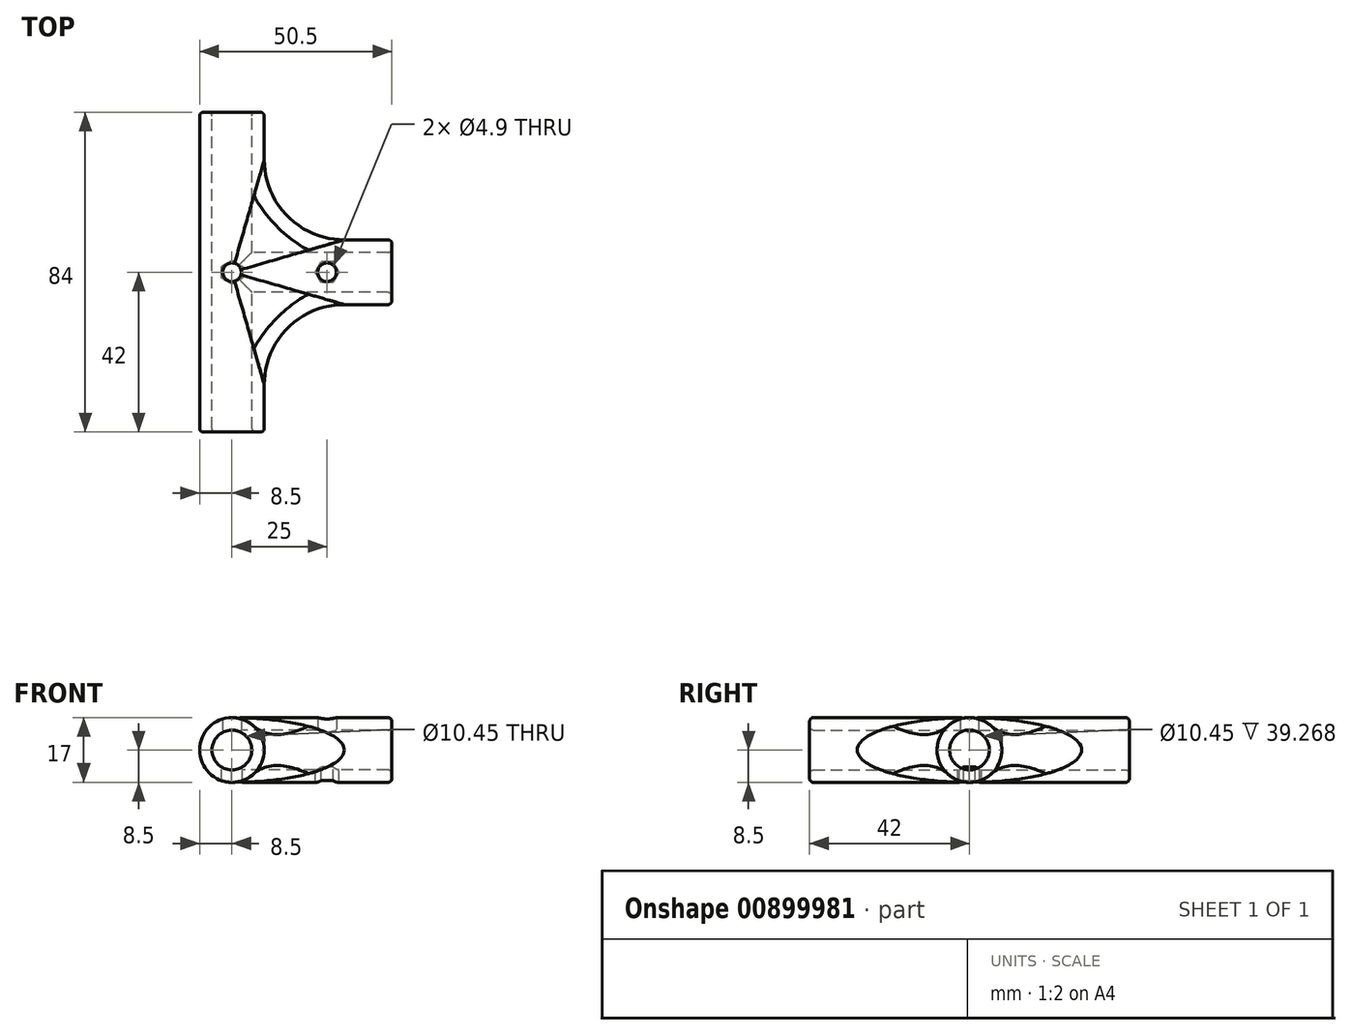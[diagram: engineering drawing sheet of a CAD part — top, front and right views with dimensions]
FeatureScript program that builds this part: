
annotation { "Feature Type Name" : "Feature", "Feature Type Description" : "" }
export const myFeature = defineFeature(function(context is Context, id is Id, definition is map)
    precondition{}
    {
        {
            assignVariable(context, id + "F0", {"name" : "longueur", "anyValue" : 84});
        }
        {
            var Q0;
            Q0=qCreatedBy(makeId("Front.planeOp"),FACE);
            var sketch = newSketch(context, id + "F1", { "sketchPlane" : qUnion([Q0])});
            skCircle(sketch, "E0", {"center": v(0, 0) * mm, "radius": 8.5 * mm});
            skCircle(sketch, "E1", {"center": v(0, 0) * mm, "radius": 5.22 * mm});
            skSolve(sketch);
        }
        {
            var Q0;
            Q0=qSketchRegion(id+"F1",true);
            extrude(context, id + "F2", {"entities" : qUnion([Q0]), "endBound" : BoundingType.SYMMETRIC, "depth" : (getVariable(context, 'longueur')) * mm, "offsetDistance" : 25 * mm});
        }
        {
            var Q0;
            Q0=qCreatedBy(makeId("Right.planeOp"),FACE);
            var sketch = newSketch(context, id + "F3", { "sketchPlane" : qUnion([Q0])});
            skCircle(sketch, "E2", {"center": v(0, 0) * mm, "radius": 8.5 * mm});
            skCircle(sketch, "E3", {"center": v(0, 0) * mm, "radius": 5.22 * mm});
            skSolve(sketch);
        }
        {
            var Q0;
            Q0=qSketchRegion(id+"F3",true);
            extrude(context, id + "F4", {"entities" : qUnion([Q0]), "operationType" : NewBodyOperationType.ADD, "depth" : (getVariable(context, 'longueur') / 2) * mm, "offsetDistance" : 25 * mm});
        }
        {
            var Q0;
            Q0=makeQuery(id+"F1.imprint","IMPRINT",FACE,{"disambiguationData":[TD([[makeQuery(id+"F1.imprint","IMPRINT",EDGE,{"derivedFrom":sQuery(id+"F1.wireOp",EDGE,"E1")}),1.0]])]});
            extrude(context, id + "F5", {"entities" : qUnion([Q0]), "operationType" : NewBodyOperationType.REMOVE, "endBound" : BoundingType.THROUGH_ALL, "oppositeDirection" : true, "depth" : 25 * mm, "offsetDistance" : 25 * mm, "hasSecondDirection" : true, "secondDirectionBound" : SecondDirectionBoundingType.THROUGH_ALL, "secondDirectionOppositeDirection" : false, "secondDirectionDepth" : 25 * mm});
        }
        {
            var Q0;
            Q0=makeQuery(id+"F3.imprint","IMPRINT",FACE,{"disambiguationData":[TD([[makeQuery(id+"F3.imprint","IMPRINT",EDGE,{"derivedFrom":sQuery(id+"F3.wireOp",EDGE,"E3")}),1.0]])]});
            extrude(context, id + "F6", {"entities" : qUnion([Q0]), "operationType" : NewBodyOperationType.REMOVE, "endBound" : BoundingType.THROUGH_ALL, "depth" : 25 * mm, "offsetDistance" : 25 * mm});
        }
        {
            var Q0;
            Q0=makeQuery(id+"F4.boolean.opBoolean","INTERSECT",EDGE,{"disambiguationData":[OD(0.0)],"derivedFrom":[makeQuery(id+"F2.opExtrude","SWEPT_FACE",FACE,{"disambiguationData":[OSD([sQuery(id+"F1.wireOp",EDGE,"E0")])]}),makeQuery(id+"F4.opExtrude","SWEPT_FACE",FACE,{"disambiguationData":[OSD([sQuery(id+"F3.wireOp",EDGE,"E2")])]})]});
            var Q1;
            Q1=makeQuery(id+"F4.boolean.opBoolean","INTERSECT",EDGE,{"disambiguationData":[OD(1.0)],"derivedFrom":[makeQuery(id+"F2.opExtrude","SWEPT_FACE",FACE,{"disambiguationData":[OSD([sQuery(id+"F1.wireOp",EDGE,"E0")])]}),makeQuery(id+"F4.opExtrude","SWEPT_FACE",FACE,{"disambiguationData":[OSD([sQuery(id+"F3.wireOp",EDGE,"E2")])]})]});
            fillet(context, id + "F7", {"entities" : qUnion([Q0, Q1]), "radius" : (getVariable(context, 'longueur') / 4) * mm, "tangentPropagation" : true, "allowEdgeOverflow" : false});
        }
        {
            var Q0;
            Q0=qCreatedBy(makeId("Top.planeOp"),FACE);
            var sketch = newSketch(context, id + "F8", { "sketchPlane" : qUnion([Q0])});
            skLineSegment(sketch, "E4", {"start": v(0, 42) * mm, "end": v(0, -42) * mm, "construction": true});
            skLineSegment(sketch, "E5", {"start": v(42, 0) * mm, "end": v(0, 0) * mm, "construction": true});
            skCircle(sketch, "E6", {"center": v(0, 0) * mm, "radius": 2.45 * mm});
            skCircle(sketch, "E7", {"center": v(25, 0) * mm, "radius": 2.45 * mm});
            skCircle(sketch, "E8.cCircle", {"center": v(0, 0) * mm, "radius": 2.7 * mm, "construction": true});
            skLineSegment(sketch, "E8.0", {"start": v(-2.7, 1.56) * mm, "end": v(0, 3.12) * mm});
            skLineSegment(sketch, "E8.1", {"start": v(0, 3.12) * mm, "end": v(2.7, 1.56) * mm});
            skLineSegment(sketch, "E8.2", {"start": v(2.7, 1.56) * mm, "end": v(2.7, -1.56) * mm});
            skLineSegment(sketch, "E8.3", {"start": v(2.7, -1.56) * mm, "end": v(0, -3.12) * mm});
            skLineSegment(sketch, "E8.4", {"start": v(0, -3.12) * mm, "end": v(-2.7, -1.56) * mm});
            skLineSegment(sketch, "E8.5", {"start": v(-2.7, -1.56) * mm, "end": v(-2.7, 1.56) * mm});
            skCircle(sketch, "E9.cCircle", {"center": v(25, 0) * mm, "radius": 2.7 * mm, "construction": true});
            skLineSegment(sketch, "E9.0", {"start": v(23.44, 2.7) * mm, "end": v(26.56, 2.7) * mm});
            skLineSegment(sketch, "E9.1", {"start": v(26.56, 2.7) * mm, "end": v(28.12, 0) * mm});
            skLineSegment(sketch, "E9.2", {"start": v(28.12, 0) * mm, "end": v(26.56, -2.7) * mm});
            skLineSegment(sketch, "E9.3", {"start": v(26.56, -2.7) * mm, "end": v(23.44, -2.7) * mm});
            skLineSegment(sketch, "E9.4", {"start": v(23.44, -2.7) * mm, "end": v(21.88, 0) * mm});
            skLineSegment(sketch, "E9.5", {"start": v(21.88, 0) * mm, "end": v(23.44, 2.7) * mm});
            skPoint(sketch, "E9.0.midPoint", {"position": v(25, 2.7) * mm});
            skLineSegment(sketch, "E10", {"start": v(5, 42) * mm, "end": v(5, -42) * mm, "construction": true});
            skSolve(sketch);
        }
        {
            var Q0;
            Q0=makeQuery(id+"F8.imprint","IMPRINT",FACE,{"disambiguationData":[TD([[makeQuery(id+"F8.imprint","IMPRINT",EDGE,{"derivedFrom":sQuery(id+"F8.wireOp",EDGE,"E7")}),-1.0]])]});
            var Q1;
            Q1=makeQuery(id+"F8.imprint","IMPRINT",FACE,{"disambiguationData":[TD([[makeQuery(id+"F8.imprint","IMPRINT",EDGE,{"derivedFrom":sQuery(id+"F8.wireOp",EDGE,"E7")}),1.0]])]});
            var Q2;
            Q2=makeQuery(id+"F8.imprint","IMPRINT",FACE,{"disambiguationData":[TD([[makeQuery(id+"F8.imprint","IMPRINT",EDGE,{"derivedFrom":sQuery(id+"F8.wireOp",EDGE,"E6")}),-1.0]])]});
            var Q3;
            Q3=makeQuery(id+"F8.imprint","IMPRINT",FACE,{"disambiguationData":[TD([[makeQuery(id+"F8.imprint","IMPRINT",EDGE,{"derivedFrom":sQuery(id+"F8.wireOp",EDGE,"E6")}),1.0]])]});
            var Q4;
            Q4=makeQuery(id+"F8.imprint","IMPRINT",FACE,{"disambiguationData":[TD([[makeQuery(id+"F8.imprint","IMPRINT",EDGE,{"derivedFrom":sQuery(id+"F8.wireOp",EDGE,"4j9zKeuf-upRM-FHdC-ZF1t-ZN2zI3ddvpTP")}),-1.0]])]});
            var Q5;
            Q5=makeQuery(id+"F8.imprint","IMPRINT",FACE,{"disambiguationData":[TD([[makeQuery(id+"F8.imprint","IMPRINT",EDGE,{"derivedFrom":sQuery(id+"F8.wireOp",EDGE,"4j9zKeuf-upRM-FHdC-ZF1t-ZN2zI3ddvpTP")}),1.0]])]});
            extrude(context, id + "F9", {"entities" : qUnion([Q0, Q1, Q2, Q3, Q4, Q5]), "operationType" : NewBodyOperationType.REMOVE, "endBound" : BoundingType.THROUGH_ALL, "oppositeDirection" : true, "depth" : 25 * mm, "offsetDistance" : 25 * mm});
        }
        {
            var Q0;
            Q0=makeQuery(id+"F8.imprint","IMPRINT",FACE,{"disambiguationData":[TD([[makeQuery(id+"F8.imprint","IMPRINT",EDGE,{"derivedFrom":sQuery(id+"F8.wireOp",EDGE,"4j9zKeuf-upRM-FHdC-ZF1t-ZN2zI3ddvpTP")}),1.0]])]});
            var Q1;
            Q1=makeQuery(id+"F8.imprint","IMPRINT",FACE,{"disambiguationData":[TD([[makeQuery(id+"F8.imprint","IMPRINT",EDGE,{"derivedFrom":sQuery(id+"F8.wireOp",EDGE,"E6")}),1.0]])]});
            var Q2;
            Q2=makeQuery(id+"F8.imprint","IMPRINT",FACE,{"disambiguationData":[TD([[makeQuery(id+"F8.imprint","IMPRINT",EDGE,{"derivedFrom":sQuery(id+"F8.wireOp",EDGE,"E7")}),1.0]])]});
            extrude(context, id + "F10", {"entities" : qUnion([Q0, Q1, Q2]), "operationType" : NewBodyOperationType.REMOVE, "endBound" : BoundingType.THROUGH_ALL, "depth" : 25 * mm, "offsetDistance" : 25 * mm});
        }
        {
            var Q0;
            Q0=makeQuery(id+"F2.opExtrude","CAP_FACE",FACE,{"disambiguationData":[OSD([sQuery(id+"F1.wireOp",EDGE,"E0"),sQuery(id+"F1.wireOp",EDGE,"E1")])],"isStart":false});
            var Q1;
            Q1=makeQuery(id+"F4.opExtrude","CAP_FACE",FACE,{"disambiguationData":[OSD([sQuery(id+"F3.wireOp",EDGE,"E2"),sQuery(id+"F3.wireOp",EDGE,"E3")])],"isStart":false});
            var Q2;
            Q2=makeQuery(id+"F2.opExtrude","CAP_FACE",FACE,{"disambiguationData":[OSD([sQuery(id+"F1.wireOp",EDGE,"E0"),sQuery(id+"F1.wireOp",EDGE,"E1")])],"isStart":true});
            fillet(context, id + "F11", {"entities" : qUnion([Q0, Q1, Q2]), "radius" : 1 * mm, "tangentPropagation" : true, "allowEdgeOverflow" : false});
        }
    });
